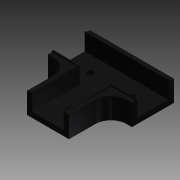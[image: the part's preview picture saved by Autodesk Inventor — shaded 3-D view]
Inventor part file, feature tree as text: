
AUTODESK INVENTOR PART (.ipt)
format: ipt  version: 2015 (Build 190159000, 159)  size: 186,368 bytes
history: native  units: in
note: dims shown in document units (in); Inventor stores cm internally (conversion verified against a paired STEP export)
features: extrude x6, sketch x6, other x3, split x1, fillet x1
ambient origin geometry x8: Origin, YZ Plane, XZ Plane, XY Plane, X Axis, Y Axis, Z Axis, Center Point
bodies: Solid1 (feature_tree)
feature tree (17):
  extrude  "Extrusion1"  Depth=1.0in
  extrude  "Extrusion2"  Depth=0.5in TaperAngle=0.0deg
  extrude  "Extrusion3"  Depth=0.5in
  extrude  "Extrusion4"  Depth=1.75in TaperAngle=0.0deg
  extrude  "Extrusion5"  Depth=0.75in
  split  "Split1"
  other  "Lip1"
  other  "Lip2"
  other  "Lip3"
  extrude  "Extrusion6"  Depth=0.375in
  fillet  "Fillet1"  Radius=1.0in
  sketch  "Sketch1"  dims[d0=1.0in d1=1.0in]
  sketch  "Sketch2"  dims[d2=2.0in d3=0.0in d4=0.5in d5=0.0in]
  sketch  "Sketch4"  dims[d6=0.5in d7=0.0in d8=0.75in]
  sketch  "Sketch5"  dims[d9=0.75in d10=1.75in d11=0.0in]
  sketch  "Sketch6"  dims[d12=0.75in d13=0.75in]
  sketch  "Sketch7"  dims[d14=1.75in d15=0.0in d16=0.03in d17=0.03in d18=0.0in d19=0.0in d20=0.0in d21=0.0in d22=0.03in d23=0.03in d24=0.0in d25=0.0in d26=0.0in d27=0.0in d28=0.03in d29=0.03in d30=0.0in d31=0.0in d32=0.0in d33=0.0in d34=0.141in d35=1.0in d36=0.0in d37=0.375in]
